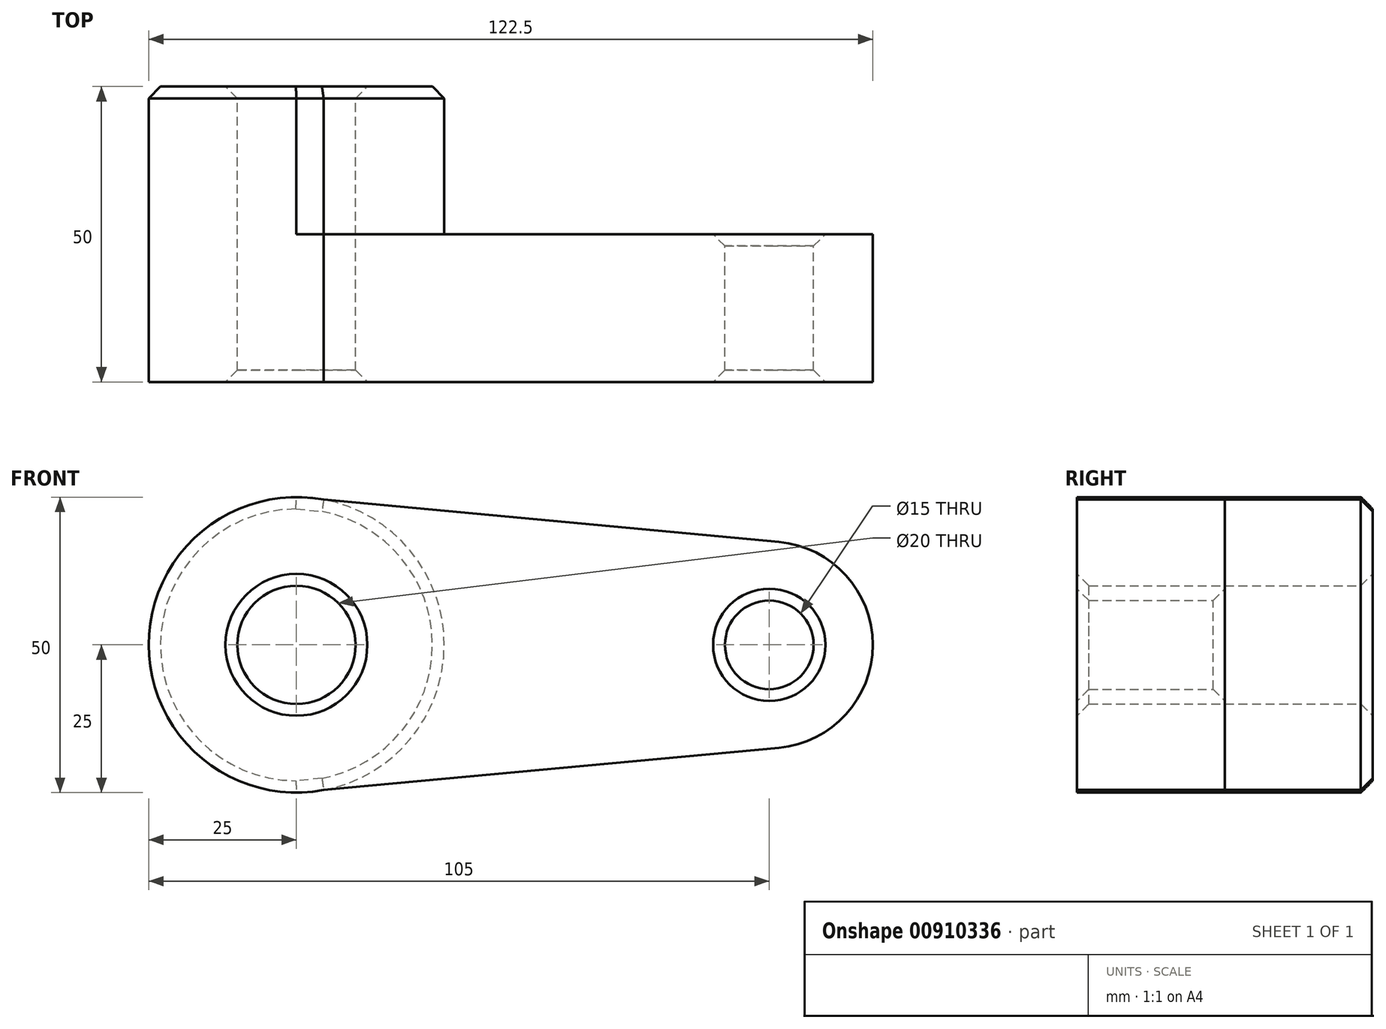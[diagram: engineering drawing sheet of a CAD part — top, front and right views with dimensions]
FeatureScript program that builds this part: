
annotation { "Feature Type Name" : "Feature", "Feature Type Description" : "" }
export const myFeature = defineFeature(function(context is Context, id is Id, definition is map)
    precondition{}
    {
        {
            var Q0;
            Q0=qCreatedBy(makeId("Front.planeOp"),FACE);
            var sketch = newSketch(context, id + "F0", { "sketchPlane" : qUnion([Q0])});
            skCircle(sketch, "E0", {"center": v(0, 0) * mm, "radius": 25 * mm});
            skCircle(sketch, "E1", {"center": v(80, 0) * mm, "radius": 17.5 * mm});
            skLineSegment(sketch, "E2", {"start": v(0, 25) * mm, "end": v(81.62, 17.43) * mm});
            skLineSegment(sketch, "E3", {"start": v(0, -25) * mm, "end": v(81.62, -17.43) * mm});
            skCircle(sketch, "E4", {"center": v(0, 0) * mm, "radius": 10 * mm});
            skCircle(sketch, "E5", {"center": v(80, 0) * mm, "radius": 7.5 * mm});
            skSolve(sketch);
        }
        {
            var Q0;
            Q0 = qSketchRegion(id + "F0", true);
            extrude(context, id + "F1", {"entities" : qUnion([Q0]), "depth" : 25 * mm, "offsetDistance" : 25 * mm});
        }
        {
            var Q0;
            Q0=makeQuery(id+"F0.imprint","IMPRINT",FACE,{"disambiguationData":[TD([[makeQuery(id+"F0.imprint","IMPRINT",EDGE,{"derivedFrom":sQuery(id+"F0.wireOp",EDGE,"E4")}),-1.0]])]});
            extrude(context, id + "F2", {"entities" : qUnion([Q0]), "operationType" : NewBodyOperationType.ADD, "oppositeDirection" : true, "depth" : 25 * mm, "offsetDistance" : 25 * mm});
        }
        {
            var Q0;
            {var subQ0=sQuery(id+"F0.wireOp",EDGE,"E0");Q0=makeQuery(id+"F2.opExtrude","CAP_EDGE",EDGE,{"disambiguationData":[OSD([subQ0]),TDD([makeQuery(id+"F0.imprint","IMPRINT",EDGE,{"disambiguationData":[TD([[makeQuery(id+"F0.imprint","INTERSECT",VERTEX,{"disambiguationData":[OD(0.0)],"derivedFrom":[subQ0,sQuery(id+"F0.wireOp",EDGE,"E2")]}),-1.0]])],"derivedFrom":subQ0})])],"isStart":false});}
            var Q1;
            {var subQ0=sQuery(id+"F0.wireOp",EDGE,"E4");Q1=makeQuery(id+"F2.boolean.opBoolean","MERGE",FACE,{"derivedFrom":[makeQuery(id+"F1.opExtrude","SWEPT_FACE",FACE,{"disambiguationData":[OSD([subQ0])]}),makeQuery(id+"F2.opExtrude","SWEPT_FACE",FACE,{"disambiguationData":[OSD([subQ0])]})]});}
            var Q2;
            Q2=makeQuery(id+"F2.opExtrude","CAP_FACE",FACE,{"disambiguationData":[OSD([sQuery(id+"F0.wireOp",EDGE,"E0"),sQuery(id+"F0.wireOp",EDGE,"E2"),sQuery(id+"F0.wireOp",EDGE,"E3"),sQuery(id+"F0.wireOp",EDGE,"E4")])],"isStart":false});
            chamfer(context, id + "F3", {"entities" : qUnion([Q0, Q1, Q2]), "width" : 2 * mm, "tangentPropagation" : true});
        }
        {
            var Q0;
            Q0=makeQuery(id+"F1.opExtrude","SWEPT_FACE",FACE,{"disambiguationData":[OSD([sQuery(id+"F0.wireOp",EDGE,"E5")])]});
            chamfer(context, id + "F4", {"entities" : qUnion([Q0]), "width" : 2 * mm, "tangentPropagation" : true});
        }
    });
